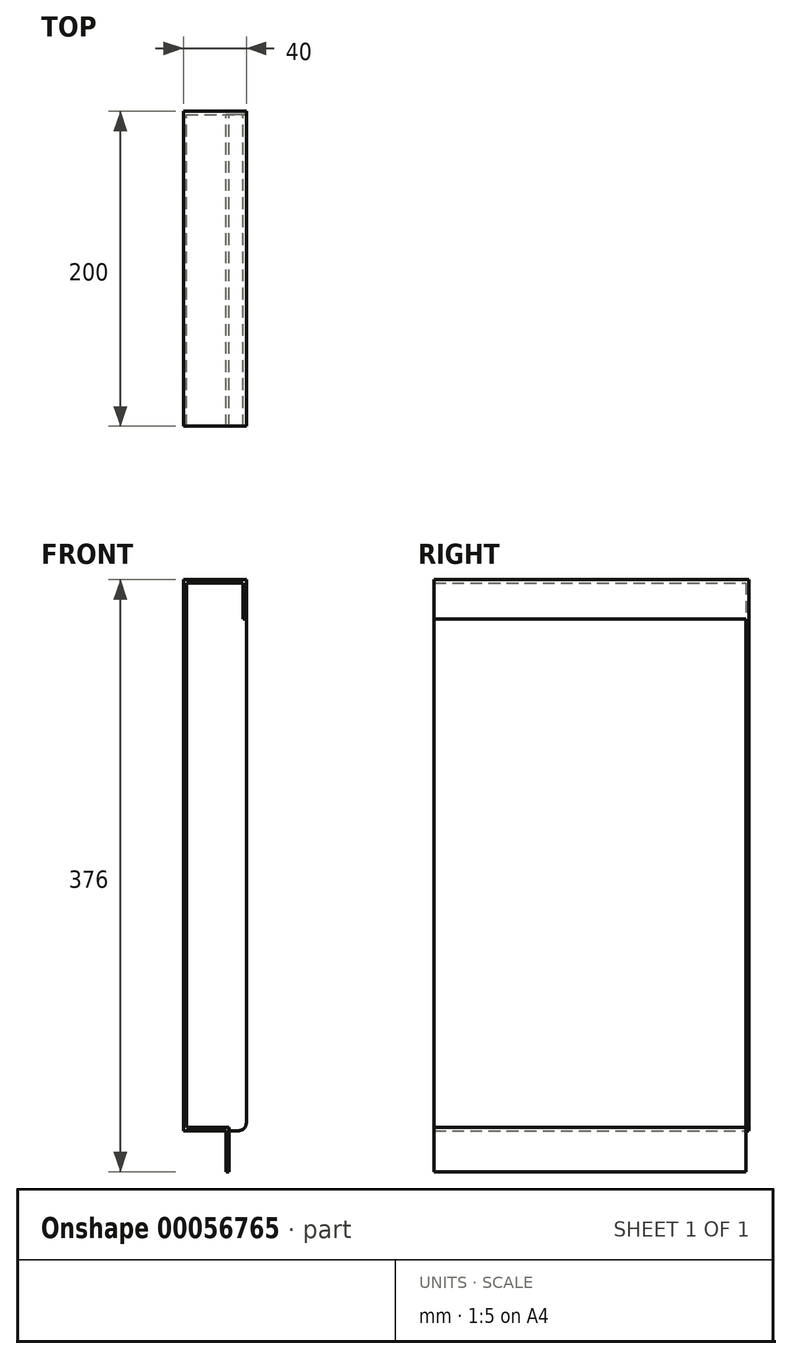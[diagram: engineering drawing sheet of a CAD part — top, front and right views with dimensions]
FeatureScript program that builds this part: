
annotation { "Feature Type Name" : "Feature", "Feature Type Description" : "" }
export const myFeature = defineFeature(function(context is Context, id is Id, definition is map)
    precondition{}
    {
        {
            var Q0;
            Q0=qCreatedBy(makeId("Front.planeOp"),FACE);
            var sketch = newSketch(context, id + "F0", { "sketchPlane" : qUnion([Q0])});
            skLineSegment(sketch, "E0", {"start": v(0, 0) * mm, "end": v(0, -350) * mm});
            skLineSegment(sketch, "E1", {"start": v(0, -350) * mm, "end": v(27, -350) * mm});
            skLineSegment(sketch, "E2", {"start": v(27, -350) * mm, "end": v(27, -376) * mm});
            skLineSegment(sketch, "E3", {"start": v(0, 0) * mm, "end": v(40, 0) * mm});
            skLineSegment(sketch, "E4", {"start": v(40, 0) * mm, "end": v(40, -25) * mm});
            skLineSegment(sketch, "E5.0", {"start": v(38, -2) * mm, "end": v(38, -25) * mm});
            skLineSegment(sketch, "E5.1", {"start": v(29, -348) * mm, "end": v(29, -376) * mm});
            skLineSegment(sketch, "E5.2", {"start": v(2, -348) * mm, "end": v(29, -348) * mm});
            skLineSegment(sketch, "E5.3", {"start": v(2, -2) * mm, "end": v(2, -348) * mm});
            skLineSegment(sketch, "E5.4", {"start": v(2, -2) * mm, "end": v(38, -2) * mm});
            skLineSegment(sketch, "E6", {"start": v(38, -25) * mm, "end": v(40, -25) * mm});
            skLineSegment(sketch, "E7", {"start": v(27, -376) * mm, "end": v(29, -376) * mm});
            skSolve(sketch);
        }
        {
            var Q0;
            Q0=qCreatedBy(makeId("Top.planeOp"),FACE);
            var sketch = newSketch(context, id + "F1", { "sketchPlane" : qUnion([Q0])});
            skLineSegment(sketch, "E8", {"start": v(0, 0) * mm, "end": v(0, 198) * mm});
            skSolve(sketch);
        }
        {
            var Q0;
            Q0=qSketchRegion(id+"F0",true);
            var Q1;
            Q1=qConstructionFilter(qBodyType(qCreatedBy(id+"F1",EDGE),BodyType.WIRE),ConstructionObject.NO);
            sweep(context, id + "F2", {"profiles" : qUnion([Q0]), "path" : qUnion([Q1])});
        }
        {
            var Q0;
            Q0=makeQuery(id+"F2.opSweep","CAP_FACE",FACE,{"disambiguationData":[OSD([sQuery(id+"F0.wireOp",EDGE,"E0"),sQuery(id+"F0.wireOp",EDGE,"E1"),sQuery(id+"F0.wireOp",EDGE,"E2"),sQuery(id+"F0.wireOp",EDGE,"E3"),sQuery(id+"F0.wireOp",EDGE,"E4"),sQuery(id+"F0.wireOp",EDGE,"E5.0"),sQuery(id+"F0.wireOp",EDGE,"E5.1"),sQuery(id+"F0.wireOp",EDGE,"E5.2"),sQuery(id+"F0.wireOp",EDGE,"E5.3"),sQuery(id+"F0.wireOp",EDGE,"E5.4"),sQuery(id+"F0.wireOp",EDGE,"E6"),sQuery(id+"F0.wireOp",EDGE,"E7"),sQuery(id+"F1.wireOp",VERTEX,"E8.end")])],"isStart":false});
            var sketch = newSketch(context, id + "F3", { "sketchPlane" : qUnion([Q0])});
            skLineSegment(sketch, "E9.0", {"start": v(0, -350) * mm, "end": v(0, 0) * mm});
            skLineSegment(sketch, "E10.0", {"start": v(-40, 0) * mm, "end": v(0, 0) * mm});
            skLineSegment(sketch, "E11.0", {"start": v(-40, -25) * mm, "end": v(-40, 0) * mm});
            skLineSegment(sketch, "E12.0", {"start": v(-40, -25) * mm, "end": v(-40, -345) * mm});
            skArc(sketch, "E13.0", {"start": v(-35, -350) * mm, "mid": v(-38.54, -348.54) * mm, "end": v(-40, -345) * mm});
            skLineSegment(sketch, "E14.0", {"start": v(-35, -350) * mm, "end": v(-29, -350) * mm});
            skLineSegment(sketch, "E15.0", {"start": v(-27, -350) * mm, "end": v(0, -350) * mm});
            skLineSegment(sketch, "E16", {"start": v(-29, -350) * mm, "end": v(-27, -350) * mm});
            skSolve(sketch);
        }
        {
            var Q0;
            Q0=qSketchRegion(id+"F3",true);
            extrude(context, id + "F4", {"entities" : qUnion([Q0]), "operationType" : NewBodyOperationType.ADD, "depth" : 2 * mm});
        }
    });
